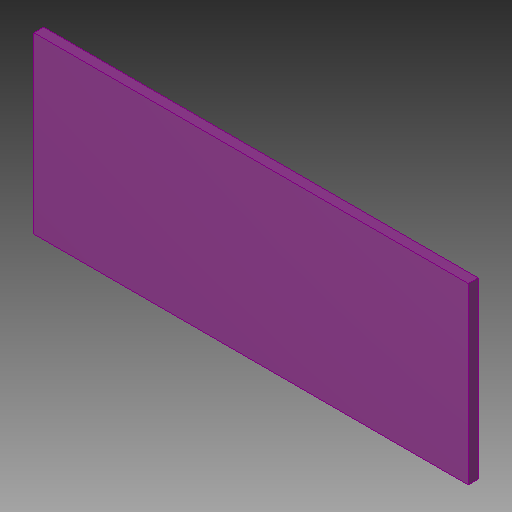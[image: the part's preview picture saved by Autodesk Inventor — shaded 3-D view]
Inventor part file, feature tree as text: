
AUTODESK INVENTOR PART (.ipt)
format: ipt  version: 2019 (Build 230136000, 136)  size: 89,600 bytes
history: native  units: in
note: dims shown in document units (in); Inventor stores cm internally (conversion verified against a paired STEP export)
features: extrude x1, other x1
ambient origin geometry x8: Origin, YZ Plane, XZ Plane, XY Plane, X Axis, Y Axis, Z Axis, Center Point
bodies: Solid1 (feature_tree)
feature tree (2):
  extrude  "Extrusion1"  Depth=0.0394in TaperAngle=0.0deg
  other  "ARDUINO-NANO-3_0, ARDUINO-NANO-3_0_10"
